# Revit family: Bath-Drop_In-KOHLER-AVEC-K-25833_1
name_source: partatom
category: Plumbing Fixtures
units: mm (PartAtom-declared; Revit-internal decimal feet)

## family parameters
Cut with Voids When Loaded = No
Host = Face
OmniClass Number = 23.31.15.00
OmniClass Title = Bathtubs
Part Type = Normal
Room Calculation Point = No
Round Connector Dimension = Use Diameter
Shared = No

## types (3) — shared parameters
ADA Compliant = No
Assembly Code = D2010500
CW Connection = No
Cold Water Inlet = Cold Water Inlet
Date Modified = 01/10/2023
Default Elevation = 0"
Description = NEW CORE 60 INCH X 42 INCH DROP IN BATH
Drain Included = No
HW Connection = No
Height = 18 1/8"
Hot Water Inlet = Hot Water Inlet
Length = 60"
Manufacturer = Kohler Co.
Master Format 2014 = 22 41 19
Master Format 2014 Name = Residential Bathtubs
Material = Acrylic
Product Documentation Link = https://www.us.kohler.com
Product Name = AVEC
Product Page URL = http://www.us.kohler.com
URL = https://www.us.kohler.com
Vent Connection = No
Waste Connection = Yes
Waste Water Outlet = Waste Water Outlet
WaterSense Certified = No
Width = 42"

## per-type parameters (varying)
| type | Finish | Model | Type |
| 0-White | KOHLER-Acrylic-0-White | K-25833-0 | 1 |
| 96-Biscuit | KOHLER-Acrylic-96-Biscuit | K-25833-96 | 2 |
| NY-Dune | KOHLER-Acrylic-NY-Dune | K-25833-NY | 3 |

## geometry (parser evidence)
native form markers: Sweep x6
no freeform markers — native parametric forms only
